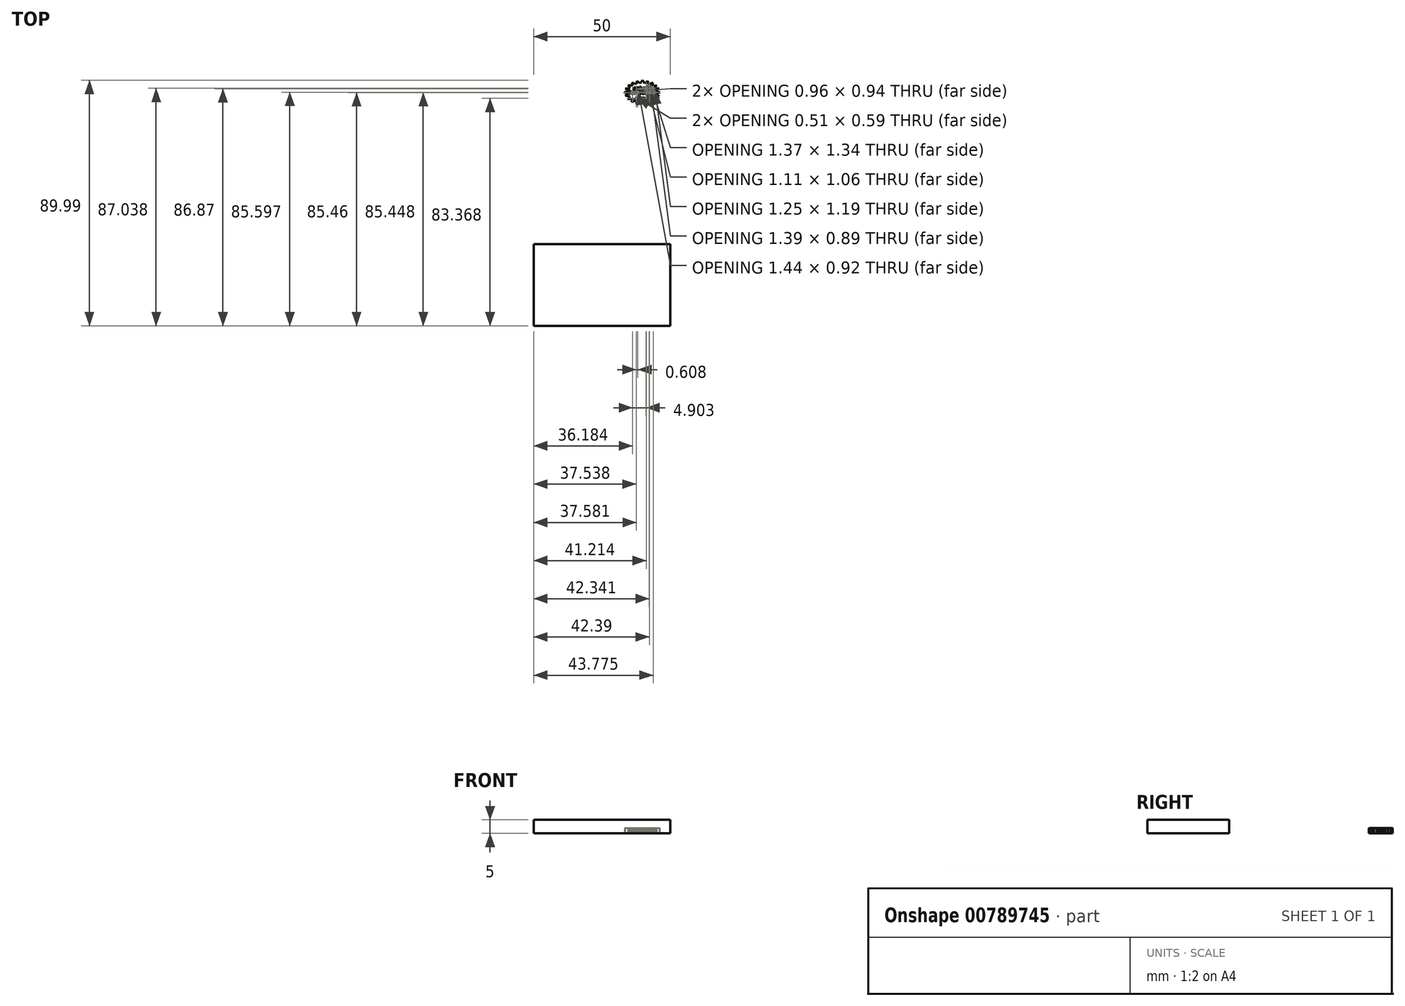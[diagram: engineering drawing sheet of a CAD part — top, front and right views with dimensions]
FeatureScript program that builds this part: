
annotation { "Feature Type Name" : "Feature", "Feature Type Description" : "" }
export const myFeature = defineFeature(function(context is Context, id is Id, definition is map)
    precondition{}
    {
        {
            var Q0;
            Q0=qCreatedBy(makeId("Top.planeOp"),FACE);
            var sketch = newSketch(context, id + "F0", { "sketchPlane" : qUnion([Q0])});
            skLineSegment(sketch, "E0.bottom", {"start": v(-29.78, 14.72) * mm, "end": v(20.22, 14.72) * mm});
            skLineSegment(sketch, "E0.top", {"start": v(-29.78, -15.28) * mm, "end": v(20.22, -15.28) * mm});
            skLineSegment(sketch, "E0.left", {"start": v(-29.78, 14.72) * mm, "end": v(-29.78, -15.28) * mm});
            skLineSegment(sketch, "E0.right", {"start": v(20.22, 14.72) * mm, "end": v(20.22, -15.28) * mm});
            skSolve(sketch);
        }
        {
            var Q0;
            Q0=makeQuery(id+"F0.imprint","IMPRINT",FACE,{"disambiguationData":[TD([[makeQuery(id+"F0.imprint","IMPRINT",EDGE,{"derivedFrom":sQuery(id+"F0.wireOp",EDGE,"E0.bottom")}),-1.0]])]});
            extrude(context, id + "F1", {"entities" : qUnion([Q0]), "depth" : 5 * mm, "offsetDistance" : 25 * mm});
        }
        {
            var Q0;
            Q0=qCreatedBy(makeId("Top.planeOp"),FACE);
            var sketch = newSketch(context, id + "F2", { "sketchPlane" : qUnion([Q0])});
            skLineSegment(sketch, "E1", {"start": v(13.24, 72.43) * mm, "end": v(12.87, 72.43) * mm});
            skLineSegment(sketch, "E2", {"start": v(12.87, 72.43) * mm, "end": v(12.56, 71.95) * mm});
            skLineSegment(sketch, "E3", {"start": v(12.56, 71.95) * mm, "end": v(12.26, 72.43) * mm});
            skLineSegment(sketch, "E4", {"start": v(12.26, 72.43) * mm, "end": v(11.88, 72.43) * mm});
            skLineSegment(sketch, "E5", {"start": v(11.88, 72.43) * mm, "end": v(12.39, 71.65) * mm});
            skLineSegment(sketch, "E6", {"start": v(12.39, 71.65) * mm, "end": v(12.39, 71.09) * mm});
            skLineSegment(sketch, "E7", {"start": v(12.39, 71.09) * mm, "end": v(12.73, 71.09) * mm});
            skLineSegment(sketch, "E8", {"start": v(12.73, 71.09) * mm, "end": v(12.73, 71.65) * mm});
            skLineSegment(sketch, "E9", {"start": v(12.73, 71.65) * mm, "end": v(13.24, 72.43) * mm});
            skFitSpline(sketch, "E10", {"points": [v(11.43, 71.89) * mm, v(11.5, 71.89) * mm, v(11.56, 71.86) * mm, v(11.6, 71.81) * mm]});
            skFitSpline(sketch, "E11", {"points": [v(11.6, 71.81) * mm, v(11.63, 71.76) * mm, v(11.65, 71.69) * mm, v(11.65, 71.59) * mm]});
            skFitSpline(sketch, "E12", {"points": [v(11.65, 71.59) * mm, v(11.65, 71.5) * mm, v(11.63, 71.42) * mm, v(11.6, 71.37) * mm]});
            skFitSpline(sketch, "E13", {"points": [v(11.6, 71.37) * mm, v(11.56, 71.32) * mm, v(11.5, 71.3) * mm, v(11.43, 71.3) * mm]});
            skFitSpline(sketch, "E14", {"points": [v(11.43, 71.3) * mm, v(11.36, 71.3) * mm, v(11.3, 71.32) * mm, v(11.27, 71.37) * mm]});
            skFitSpline(sketch, "E15", {"points": [v(11.27, 71.37) * mm, v(11.23, 71.42) * mm, v(11.22, 71.5) * mm, v(11.22, 71.59) * mm]});
            skFitSpline(sketch, "E16", {"points": [v(11.22, 71.59) * mm, v(11.22, 71.69) * mm, v(11.23, 71.76) * mm, v(11.27, 71.81) * mm]});
            skFitSpline(sketch, "E17", {"points": [v(11.27, 71.81) * mm, v(11.3, 71.86) * mm, v(11.36, 71.89) * mm, v(11.43, 71.89) * mm]});
            skFitSpline(sketch, "E18", {"points": [v(11.43, 72.12) * mm, v(11.26, 72.12) * mm, v(11.12, 72.07) * mm, v(11.03, 71.98) * mm]});
            skFitSpline(sketch, "E19", {"points": [v(11.03, 71.98) * mm, v(10.93, 71.88) * mm, v(10.88, 71.75) * mm, v(10.88, 71.59) * mm]});
            skFitSpline(sketch, "E20", {"points": [v(10.88, 71.59) * mm, v(10.88, 71.42) * mm, v(10.93, 71.3) * mm, v(11.03, 71.2) * mm]});
            skFitSpline(sketch, "E21", {"points": [v(11.03, 71.2) * mm, v(11.12, 71.1) * mm, v(11.26, 71.06) * mm, v(11.43, 71.06) * mm]});
            skFitSpline(sketch, "E22", {"points": [v(11.43, 71.06) * mm, v(11.6, 71.06) * mm, v(11.74, 71.1) * mm, v(11.84, 71.2) * mm]});
            skFitSpline(sketch, "E23", {"points": [v(11.84, 71.2) * mm, v(11.94, 71.3) * mm, v(11.99, 71.42) * mm, v(11.99, 71.59) * mm]});
            skFitSpline(sketch, "E24", {"points": [v(11.99, 71.59) * mm, v(11.99, 71.75) * mm, v(11.94, 71.88) * mm, v(11.84, 71.98) * mm]});
            skFitSpline(sketch, "E25", {"points": [v(11.84, 71.98) * mm, v(11.74, 72.07) * mm, v(11.6, 72.12) * mm, v(11.43, 72.12) * mm]});
            skLineSegment(sketch, "E26", {"start": v(10.66, 71.48) * mm, "end": v(10.66, 72.1) * mm});
            skLineSegment(sketch, "E27", {"start": v(10.66, 72.1) * mm, "end": v(10.34, 72.1) * mm});
            skLineSegment(sketch, "E28", {"start": v(10.34, 72.1) * mm, "end": v(10.34, 72) * mm});
            skFitSpline(sketch, "E29", {"points": [v(10.34, 72) * mm, v(10.34, 71.94) * mm, v(10.34, 71.87) * mm, v(10.34, 71.79) * mm]});
            skFitSpline(sketch, "E30", {"points": [v(10.34, 71.79) * mm, v(10.34, 71.7) * mm, v(10.34, 71.65) * mm, v(10.34, 71.62) * mm]});
            skFitSpline(sketch, "E31", {"points": [v(10.34, 71.62) * mm, v(10.34, 71.54) * mm, v(10.34, 71.48) * mm, v(10.33, 71.45) * mm]});
            skFitSpline(sketch, "E32", {"points": [v(10.33, 71.45) * mm, v(10.33, 71.41) * mm, v(10.32, 71.39) * mm, v(10.3, 71.37) * mm]});
            skFitSpline(sketch, "E33", {"points": [v(10.3, 71.37) * mm, v(10.3, 71.35) * mm, v(10.28, 71.33) * mm, v(10.26, 71.32) * mm]});
            skFitSpline(sketch, "E34", {"points": [v(10.26, 71.32) * mm, v(10.24, 71.31) * mm, v(10.21, 71.3) * mm, v(10.19, 71.3) * mm]});
            skFitSpline(sketch, "E35", {"points": [v(10.19, 71.3) * mm, v(10.12, 71.3) * mm, v(10.07, 71.33) * mm, v(10.03, 71.38) * mm]});
            skFitSpline(sketch, "E36", {"points": [v(10.03, 71.38) * mm, v(9.99, 71.43) * mm, v(9.97, 71.5) * mm, v(9.97, 71.6) * mm]});
            skLineSegment(sketch, "E37", {"start": v(9.97, 71.6) * mm, "end": v(9.97, 72.1) * mm});
            skLineSegment(sketch, "E38", {"start": v(9.97, 72.1) * mm, "end": v(9.65, 72.1) * mm});
            skLineSegment(sketch, "E39", {"start": v(9.65, 72.1) * mm, "end": v(9.65, 71.09) * mm});
            skLineSegment(sketch, "E40", {"start": v(9.65, 71.09) * mm, "end": v(9.97, 71.09) * mm});
            skLineSegment(sketch, "E41", {"start": v(9.97, 71.09) * mm, "end": v(9.97, 71.23) * mm});
            skFitSpline(sketch, "E42", {"points": [v(9.97, 71.23) * mm, v(10.02, 71.18) * mm, v(10.07, 71.13) * mm, v(10.12, 71.1) * mm]});
            skFitSpline(sketch, "E43", {"points": [v(10.12, 71.1) * mm, v(10.18, 71.08) * mm, v(10.24, 71.06) * mm, v(10.3, 71.06) * mm]});
            skFitSpline(sketch, "E44", {"points": [v(10.3, 71.06) * mm, v(10.42, 71.06) * mm, v(10.5, 71.1) * mm, v(10.57, 71.17) * mm]});
            skFitSpline(sketch, "E45", {"points": [v(10.57, 71.17) * mm, v(10.63, 71.24) * mm, v(10.66, 71.34) * mm, v(10.66, 71.48) * mm]});
            skLineSegment(sketch, "E46", {"start": v(9.1, 72.43) * mm, "end": v(9.1, 71.93) * mm});
            skLineSegment(sketch, "E47", {"start": v(9.1, 71.93) * mm, "end": v(9.32, 71.93) * mm});
            skLineSegment(sketch, "E48", {"start": v(9.32, 71.93) * mm, "end": v(9.32, 72.43) * mm});
            skLineSegment(sketch, "E49", {"start": v(9.32, 72.43) * mm, "end": v(9.1, 72.43) * mm});
            skFitSpline(sketch, "E50", {"points": [v(8.03, 71.82) * mm, v(8.06, 71.83) * mm, v(8.09, 71.84) * mm, v(8.11, 71.85) * mm]});
            skFitSpline(sketch, "E51", {"points": [v(8.11, 71.85) * mm, v(8.14, 71.85) * mm, v(8.17, 71.86) * mm, v(8.2, 71.86) * mm]});
            skFitSpline(sketch, "E52", {"points": [v(8.2, 71.86) * mm, v(8.28, 71.86) * mm, v(8.34, 71.83) * mm, v(8.39, 71.78) * mm]});
            skFitSpline(sketch, "E53", {"points": [v(8.39, 71.78) * mm, v(8.43, 71.73) * mm, v(8.45, 71.65) * mm, v(8.45, 71.55) * mm]});
            skLineSegment(sketch, "E54", {"start": v(8.45, 71.55) * mm, "end": v(8.45, 71.09) * mm});
            skLineSegment(sketch, "E55", {"start": v(8.45, 71.09) * mm, "end": v(8.78, 71.09) * mm});
            skLineSegment(sketch, "E56", {"start": v(8.78, 71.09) * mm, "end": v(8.78, 72.1) * mm});
            skLineSegment(sketch, "E57", {"start": v(8.78, 72.1) * mm, "end": v(8.45, 72.1) * mm});
            skLineSegment(sketch, "E58", {"start": v(8.45, 72.1) * mm, "end": v(8.45, 71.93) * mm});
            skFitSpline(sketch, "E59", {"points": [v(8.45, 71.93) * mm, v(8.41, 72) * mm, v(8.37, 72.04) * mm, v(8.31, 72.07) * mm]});
            skFitSpline(sketch, "E60", {"points": [v(8.31, 72.07) * mm, v(8.26, 72.1) * mm, v(8.2, 72.12) * mm, v(8.12, 72.12) * mm]});
            skFitSpline(sketch, "E61", {"points": [v(8.12, 72.12) * mm, v(8.1, 72.12) * mm, v(8.1, 72.12) * mm, v(8.09, 72.12) * mm]});
            skFitSpline(sketch, "E62", {"points": [v(8.09, 72.12) * mm, v(8.07, 72.11) * mm, v(8.05, 72.11) * mm, v(8.03, 72.1) * mm]});
            skLineSegment(sketch, "E63", {"start": v(8.03, 72.1) * mm, "end": v(8.03, 71.82) * mm});
            skLineSegment(sketch, "E64", {"start": v(6.87, 71.6) * mm, "end": v(6.87, 71.5) * mm});
            skLineSegment(sketch, "E65", {"start": v(6.87, 71.5) * mm, "end": v(7.62, 71.5) * mm});
            skFitSpline(sketch, "E66", {"points": [v(7.62, 71.5) * mm, v(7.6, 71.43) * mm, v(7.58, 71.37) * mm, v(7.53, 71.33) * mm]});
            skFitSpline(sketch, "E67", {"points": [v(7.53, 71.33) * mm, v(7.49, 71.3) * mm, v(7.42, 71.28) * mm, v(7.34, 71.28) * mm]});
            skFitSpline(sketch, "E68", {"points": [v(7.34, 71.28) * mm, v(7.27, 71.28) * mm, v(7.2, 71.29) * mm, v(7.13, 71.3) * mm]});
            skFitSpline(sketch, "E69", {"points": [v(7.13, 71.3) * mm, v(7.06, 71.33) * mm, v(6.99, 71.36) * mm, v(6.91, 71.4) * mm]});
            skLineSegment(sketch, "E70", {"start": v(6.91, 71.4) * mm, "end": v(6.91, 71.15) * mm});
            skFitSpline(sketch, "E71", {"points": [v(6.91, 71.15) * mm, v(6.99, 71.12) * mm, v(7.07, 71.1) * mm, v(7.14, 71.09) * mm]});
            skFitSpline(sketch, "E72", {"points": [v(7.14, 71.09) * mm, v(7.22, 71.07) * mm, v(7.3, 71.06) * mm, v(7.37, 71.06) * mm]});
            skFitSpline(sketch, "E73", {"points": [v(7.37, 71.06) * mm, v(7.55, 71.06) * mm, v(7.7, 71.1) * mm, v(7.8, 71.2) * mm]});
            skFitSpline(sketch, "E74", {"points": [v(7.8, 71.2) * mm, v(7.9, 71.3) * mm, v(7.94, 71.42) * mm, v(7.94, 71.59) * mm]});
            skFitSpline(sketch, "E75", {"points": [v(7.94, 71.59) * mm, v(7.94, 71.75) * mm, v(7.9, 71.88) * mm, v(7.8, 71.98) * mm]});
            skFitSpline(sketch, "E76", {"points": [v(7.8, 71.98) * mm, v(7.7, 72.07) * mm, v(7.56, 72.12) * mm, v(7.39, 72.12) * mm]});
            skFitSpline(sketch, "E77", {"points": [v(7.39, 72.12) * mm, v(7.23, 72.12) * mm, v(7.1, 72.07) * mm, v(7, 71.97) * mm]});
            skFitSpline(sketch, "E78", {"points": [v(7, 71.97) * mm, v(6.91, 71.88) * mm, v(6.87, 71.75) * mm, v(6.87, 71.6) * mm]});
            skFitSpline(sketch, "E79", {"points": [v(7.2, 71.7) * mm, v(7.2, 71.76) * mm, v(7.21, 71.81) * mm, v(7.25, 71.85) * mm]});
            skFitSpline(sketch, "E80", {"points": [v(7.25, 71.85) * mm, v(7.28, 71.88) * mm, v(7.33, 71.9) * mm, v(7.39, 71.9) * mm]});
            skFitSpline(sketch, "E81", {"points": [v(7.39, 71.9) * mm, v(7.45, 71.9) * mm, v(7.5, 71.89) * mm, v(7.54, 71.85) * mm]});
            skFitSpline(sketch, "E82", {"points": [v(7.54, 71.85) * mm, v(7.58, 71.82) * mm, v(7.6, 71.77) * mm, v(7.61, 71.7) * mm]});
            skLineSegment(sketch, "E83", {"start": v(7.61, 71.7) * mm, "end": v(7.2, 71.7) * mm});
            skLineSegment(sketch, "E84", {"start": v(15.2, 67.7) * mm, "end": v(13.44, 67.93) * mm});
            skLineSegment(sketch, "E85", {"start": v(13.44, 67.93) * mm, "end": v(13.75, 66.73) * mm});
            skLineSegment(sketch, "E86", {"start": v(13.75, 66.73) * mm, "end": v(12.18, 67.32) * mm});
            skLineSegment(sketch, "E87", {"start": v(12.18, 67.32) * mm, "end": v(11.92, 66.12) * mm});
            skLineSegment(sketch, "E88", {"start": v(11.92, 66.12) * mm, "end": v(10.7, 67) * mm});
            skLineSegment(sketch, "E89", {"start": v(10.7, 67) * mm, "end": v(9.9, 65.92) * mm});
            skLineSegment(sketch, "E90", {"start": v(9.9, 65.92) * mm, "end": v(9.14, 67.02) * mm});
            skLineSegment(sketch, "E91", {"start": v(9.14, 67.02) * mm, "end": v(7.9, 66.15) * mm});
            skLineSegment(sketch, "E92", {"start": v(7.9, 66.15) * mm, "end": v(7.67, 67.35) * mm});
            skLineSegment(sketch, "E93", {"start": v(7.67, 67.35) * mm, "end": v(6.08, 66.78) * mm});
            skLineSegment(sketch, "E94", {"start": v(6.08, 66.78) * mm, "end": v(6.43, 67.97) * mm});
            skLineSegment(sketch, "E95", {"start": v(6.43, 67.97) * mm, "end": v(4.65, 67.76) * mm});
            skLineSegment(sketch, "E96", {"start": v(4.65, 67.76) * mm, "end": v(5.53, 68.82) * mm});
            skLineSegment(sketch, "E97", {"start": v(5.53, 68.82) * mm, "end": v(3.74, 69) * mm});
            skLineSegment(sketch, "E98", {"start": v(3.74, 69) * mm, "end": v(5.06, 69.82) * mm});
            skLineSegment(sketch, "E99", {"start": v(5.06, 69.82) * mm, "end": v(3.44, 70.36) * mm});
            skLineSegment(sketch, "E100", {"start": v(3.44, 70.36) * mm, "end": v(5.08, 70.87) * mm});
            skLineSegment(sketch, "E101", {"start": v(5.08, 70.87) * mm, "end": v(3.78, 71.71) * mm});
            skLineSegment(sketch, "E102", {"start": v(3.78, 71.71) * mm, "end": v(5.57, 71.86) * mm});
            skLineSegment(sketch, "E103", {"start": v(5.57, 71.86) * mm, "end": v(4.73, 72.93) * mm});
            skLineSegment(sketch, "E104", {"start": v(4.73, 72.93) * mm, "end": v(6.5, 72.7) * mm});
            skLineSegment(sketch, "E105", {"start": v(6.5, 72.7) * mm, "end": v(6.18, 73.9) * mm});
            skLineSegment(sketch, "E106", {"start": v(6.18, 73.9) * mm, "end": v(7.76, 73.3) * mm});
            skLineSegment(sketch, "E107", {"start": v(7.76, 73.3) * mm, "end": v(8.01, 74.5) * mm});
            skLineSegment(sketch, "E108", {"start": v(8.01, 74.5) * mm, "end": v(9.24, 73.62) * mm});
            skLineSegment(sketch, "E109", {"start": v(9.24, 73.62) * mm, "end": v(10.03, 74.7) * mm});
            skLineSegment(sketch, "E110", {"start": v(10.03, 74.7) * mm, "end": v(10.8, 73.6) * mm});
            skLineSegment(sketch, "E111", {"start": v(10.8, 73.6) * mm, "end": v(12.05, 74.48) * mm});
            skLineSegment(sketch, "E112", {"start": v(12.05, 74.48) * mm, "end": v(12.26, 73.27) * mm});
            skLineSegment(sketch, "E113", {"start": v(12.26, 73.27) * mm, "end": v(13.86, 73.84) * mm});
            skLineSegment(sketch, "E114", {"start": v(13.86, 73.84) * mm, "end": v(13.5, 72.65) * mm});
            skLineSegment(sketch, "E115", {"start": v(13.5, 72.65) * mm, "end": v(15.29, 72.86) * mm});
            skLineSegment(sketch, "E116", {"start": v(15.29, 72.86) * mm, "end": v(14.4, 71.8) * mm});
            skLineSegment(sketch, "E117", {"start": v(14.4, 71.8) * mm, "end": v(16.2, 71.63) * mm});
            skLineSegment(sketch, "E118", {"start": v(16.2, 71.63) * mm, "end": v(14.87, 70.8) * mm});
            skLineSegment(sketch, "E119", {"start": v(14.87, 70.8) * mm, "end": v(16.5, 70.27) * mm});
            skLineSegment(sketch, "E120", {"start": v(16.5, 70.27) * mm, "end": v(14.86, 69.76) * mm});
            skLineSegment(sketch, "E121", {"start": v(14.86, 69.76) * mm, "end": v(16.15, 68.91) * mm});
            skLineSegment(sketch, "E122", {"start": v(16.15, 68.91) * mm, "end": v(14.37, 68.77) * mm});
            skLineSegment(sketch, "E123", {"start": v(14.37, 68.77) * mm, "end": v(15.2, 67.7) * mm});
            skLineSegment(sketch, "E124", {"start": v(13.75, 69.94) * mm, "end": v(14.23, 69.94) * mm});
            skLineSegment(sketch, "E125", {"start": v(14.23, 69.94) * mm, "end": v(14.3, 69.72) * mm});
            skLineSegment(sketch, "E126", {"start": v(14.3, 69.72) * mm, "end": v(14.62, 69.72) * mm});
            skLineSegment(sketch, "E127", {"start": v(14.62, 69.72) * mm, "end": v(14.18, 70.91) * mm});
            skLineSegment(sketch, "E128", {"start": v(14.18, 70.91) * mm, "end": v(13.81, 70.91) * mm});
            skLineSegment(sketch, "E129", {"start": v(13.81, 70.91) * mm, "end": v(13.37, 69.72) * mm});
            skLineSegment(sketch, "E130", {"start": v(13.37, 69.72) * mm, "end": v(13.68, 69.72) * mm});
            skLineSegment(sketch, "E131", {"start": v(13.68, 69.72) * mm, "end": v(13.75, 69.94) * mm});
            skLineSegment(sketch, "E132", {"start": v(14.16, 70.16) * mm, "end": v(13.83, 70.16) * mm});
            skLineSegment(sketch, "E133", {"start": v(13.83, 70.16) * mm, "end": v(14, 70.63) * mm});
            skLineSegment(sketch, "E134", {"start": v(14, 70.63) * mm, "end": v(14.16, 70.16) * mm});
            skLineSegment(sketch, "E135", {"start": v(13.3, 70.61) * mm, "end": v(13.03, 70.61) * mm});
            skLineSegment(sketch, "E136", {"start": v(13.03, 70.61) * mm, "end": v(12.88, 70) * mm});
            skLineSegment(sketch, "E137", {"start": v(12.88, 70) * mm, "end": v(12.73, 70.61) * mm});
            skLineSegment(sketch, "E138", {"start": v(12.73, 70.61) * mm, "end": v(12.5, 70.61) * mm});
            skLineSegment(sketch, "E139", {"start": v(12.5, 70.61) * mm, "end": v(12.34, 70) * mm});
            skLineSegment(sketch, "E140", {"start": v(12.34, 70) * mm, "end": v(12.2, 70.61) * mm});
            skLineSegment(sketch, "E141", {"start": v(12.2, 70.61) * mm, "end": v(11.91, 70.61) * mm});
            skLineSegment(sketch, "E142", {"start": v(11.91, 70.61) * mm, "end": v(12.15, 69.72) * mm});
            skLineSegment(sketch, "E143", {"start": v(12.15, 69.72) * mm, "end": v(12.46, 69.72) * mm});
            skLineSegment(sketch, "E144", {"start": v(12.46, 69.72) * mm, "end": v(12.61, 70.34) * mm});
            skLineSegment(sketch, "E145", {"start": v(12.61, 70.34) * mm, "end": v(12.76, 69.72) * mm});
            skLineSegment(sketch, "E146", {"start": v(12.76, 69.72) * mm, "end": v(13.07, 69.72) * mm});
            skLineSegment(sketch, "E147", {"start": v(13.07, 69.72) * mm, "end": v(13.3, 70.61) * mm});
            skLineSegment(sketch, "E148", {"start": v(10.83, 70.17) * mm, "end": v(10.83, 70.09) * mm});
            skLineSegment(sketch, "E149", {"start": v(10.83, 70.09) * mm, "end": v(11.5, 70.09) * mm});
            skFitSpline(sketch, "E150", {"points": [v(11.5, 70.09) * mm, v(11.49, 70.02) * mm, v(11.46, 69.97) * mm, v(11.42, 69.94) * mm]});
            skFitSpline(sketch, "E151", {"points": [v(11.42, 69.94) * mm, v(11.38, 69.9) * mm, v(11.32, 69.89) * mm, v(11.25, 69.89) * mm]});
            skFitSpline(sketch, "E152", {"points": [v(11.25, 69.89) * mm, v(11.19, 69.89) * mm, v(11.13, 69.9) * mm, v(11.06, 69.91) * mm]});
            skFitSpline(sketch, "E153", {"points": [v(11.06, 69.91) * mm, v(11, 69.93) * mm, v(10.94, 69.96) * mm, v(10.87, 70) * mm]});
            skLineSegment(sketch, "E154", {"start": v(10.87, 70) * mm, "end": v(10.87, 69.78) * mm});
            skFitSpline(sketch, "E155", {"points": [v(10.87, 69.78) * mm, v(10.94, 69.75) * mm, v(11, 69.73) * mm, v(11.07, 69.72) * mm]});
            skFitSpline(sketch, "E156", {"points": [v(11.07, 69.72) * mm, v(11.14, 69.7) * mm, v(11.2, 69.7) * mm, v(11.28, 69.7) * mm]});
            skFitSpline(sketch, "E157", {"points": [v(11.28, 69.7) * mm, v(11.44, 69.7) * mm, v(11.56, 69.74) * mm, v(11.65, 69.82) * mm]});
            skFitSpline(sketch, "E158", {"points": [v(11.65, 69.82) * mm, v(11.74, 69.9) * mm, v(11.79, 70.02) * mm, v(11.79, 70.17) * mm]});
            skFitSpline(sketch, "E159", {"points": [v(11.79, 70.17) * mm, v(11.79, 70.31) * mm, v(11.74, 70.43) * mm, v(11.65, 70.51) * mm]});
            skFitSpline(sketch, "E160", {"points": [v(11.65, 70.51) * mm, v(11.57, 70.6) * mm, v(11.45, 70.64) * mm, v(11.3, 70.64) * mm]});
            skFitSpline(sketch, "E161", {"points": [v(11.3, 70.64) * mm, v(11.15, 70.64) * mm, v(11.04, 70.6) * mm, v(10.95, 70.5) * mm]});
            skFitSpline(sketch, "E162", {"points": [v(10.95, 70.5) * mm, v(10.87, 70.42) * mm, v(10.83, 70.31) * mm, v(10.83, 70.17) * mm]});
            skFitSpline(sketch, "E163", {"points": [v(11.12, 70.27) * mm, v(11.12, 70.32) * mm, v(11.14, 70.36) * mm, v(11.17, 70.4) * mm]});
            skFitSpline(sketch, "E164", {"points": [v(11.17, 70.4) * mm, v(11.2, 70.43) * mm, v(11.24, 70.45) * mm, v(11.3, 70.45) * mm]});
            skFitSpline(sketch, "E165", {"points": [v(11.3, 70.45) * mm, v(11.35, 70.45) * mm, v(11.4, 70.43) * mm, v(11.43, 70.4) * mm]});
            skFitSpline(sketch, "E166", {"points": [v(11.43, 70.4) * mm, v(11.46, 70.37) * mm, v(11.48, 70.32) * mm, v(11.5, 70.27) * mm]});
            skLineSegment(sketch, "E167", {"start": v(11.5, 70.27) * mm, "end": v(11.12, 70.27) * mm});
            skLineSegment(sketch, "E168", {"start": v(9.92, 70.59) * mm, "end": v(9.92, 70.37) * mm});
            skFitSpline(sketch, "E169", {"points": [v(9.92, 70.37) * mm, v(9.98, 70.4) * mm, v(10.04, 70.41) * mm, v(10.1, 70.43) * mm]});
            skFitSpline(sketch, "E170", {"points": [v(10.1, 70.43) * mm, v(10.15, 70.44) * mm, v(10.2, 70.45) * mm, v(10.25, 70.45) * mm]});
            skFitSpline(sketch, "E171", {"points": [v(10.25, 70.45) * mm, v(10.3, 70.45) * mm, v(10.35, 70.44) * mm, v(10.37, 70.43) * mm]});
            skFitSpline(sketch, "E172", {"points": [v(10.37, 70.43) * mm, v(10.4, 70.41) * mm, v(10.41, 70.4) * mm, v(10.41, 70.36) * mm]});
            skFitSpline(sketch, "E173", {"points": [v(10.41, 70.36) * mm, v(10.41, 70.34) * mm, v(10.4, 70.32) * mm, v(10.38, 70.31) * mm]});
            skFitSpline(sketch, "E174", {"points": [v(10.38, 70.31) * mm, v(10.36, 70.3) * mm, v(10.33, 70.29) * mm, v(10.28, 70.28) * mm]});
            skLineSegment(sketch, "E175", {"start": v(10.28, 70.28) * mm, "end": v(10.23, 70.28) * mm});
            skFitSpline(sketch, "E176", {"points": [v(10.23, 70.28) * mm, v(10.08, 70.26) * mm, v(9.98, 70.23) * mm, v(9.93, 70.19) * mm]});
            skFitSpline(sketch, "E177", {"points": [v(9.93, 70.19) * mm, v(9.88, 70.14) * mm, v(9.86, 70.08) * mm, v(9.86, 69.99) * mm]});
            skFitSpline(sketch, "E178", {"points": [v(9.86, 69.99) * mm, v(9.86, 69.89) * mm, v(9.9, 69.82) * mm, v(9.96, 69.77) * mm]});
            skFitSpline(sketch, "E179", {"points": [v(9.96, 69.77) * mm, v(10.03, 69.72) * mm, v(10.14, 69.7) * mm, v(10.28, 69.7) * mm]});
            skFitSpline(sketch, "E180", {"points": [v(10.28, 69.7) * mm, v(10.33, 69.7) * mm, v(10.4, 69.7) * mm, v(10.46, 69.71) * mm]});
            skFitSpline(sketch, "E181", {"points": [v(10.46, 69.71) * mm, v(10.52, 69.72) * mm, v(10.59, 69.74) * mm, v(10.65, 69.75) * mm]});
            skLineSegment(sketch, "E182", {"start": v(10.65, 69.75) * mm, "end": v(10.65, 69.97) * mm});
            skFitSpline(sketch, "E183", {"points": [v(10.65, 69.97) * mm, v(10.6, 69.94) * mm, v(10.54, 69.92) * mm, v(10.48, 69.9) * mm]});
            skFitSpline(sketch, "E184", {"points": [v(10.48, 69.9) * mm, v(10.42, 69.9) * mm, v(10.36, 69.89) * mm, v(10.3, 69.89) * mm]});
            skFitSpline(sketch, "E185", {"points": [v(10.3, 69.89) * mm, v(10.24, 69.89) * mm, v(10.2, 69.9) * mm, v(10.17, 69.91) * mm]});
            skFitSpline(sketch, "E186", {"points": [v(10.17, 69.91) * mm, v(10.14, 69.93) * mm, v(10.13, 69.95) * mm, v(10.13, 69.98) * mm]});
            skFitSpline(sketch, "E187", {"points": [v(10.13, 69.98) * mm, v(10.13, 70) * mm, v(10.14, 70.02) * mm, v(10.16, 70.04) * mm]});
            skFitSpline(sketch, "E188", {"points": [v(10.16, 70.04) * mm, v(10.18, 70.05) * mm, v(10.21, 70.06) * mm, v(10.27, 70.07) * mm]});
            skLineSegment(sketch, "E189", {"start": v(10.27, 70.07) * mm, "end": v(10.32, 70.07) * mm});
            skFitSpline(sketch, "E190", {"points": [v(10.32, 70.07) * mm, v(10.45, 70.09) * mm, v(10.54, 70.12) * mm, v(10.59, 70.16) * mm]});
            skFitSpline(sketch, "E191", {"points": [v(10.59, 70.16) * mm, v(10.64, 70.2) * mm, v(10.67, 70.27) * mm, v(10.67, 70.36) * mm]});
            skFitSpline(sketch, "E192", {"points": [v(10.67, 70.36) * mm, v(10.67, 70.45) * mm, v(10.63, 70.52) * mm, v(10.57, 70.57) * mm]});
            skFitSpline(sketch, "E193", {"points": [v(10.57, 70.57) * mm, v(10.5, 70.61) * mm, v(10.4, 70.64) * mm, v(10.27, 70.64) * mm]});
            skFitSpline(sketch, "E194", {"points": [v(10.27, 70.64) * mm, v(10.22, 70.64) * mm, v(10.16, 70.63) * mm, v(10.1, 70.62) * mm]});
            skFitSpline(sketch, "E195", {"points": [v(10.1, 70.62) * mm, v(10.05, 70.62) * mm, v(9.98, 70.6) * mm, v(9.92, 70.59) * mm]});
            skFitSpline(sketch, "E196", {"points": [v(9.22, 70.43) * mm, v(9.28, 70.43) * mm, v(9.33, 70.4) * mm, v(9.36, 70.36) * mm]});
            skFitSpline(sketch, "E197", {"points": [v(9.36, 70.36) * mm, v(9.4, 70.32) * mm, v(9.41, 70.25) * mm, v(9.41, 70.17) * mm]});
            skFitSpline(sketch, "E198", {"points": [v(9.41, 70.17) * mm, v(9.41, 70.08) * mm, v(9.4, 70.02) * mm, v(9.36, 69.97) * mm]});
            skFitSpline(sketch, "E199", {"points": [v(9.36, 69.97) * mm, v(9.33, 69.93) * mm, v(9.28, 69.9) * mm, v(9.22, 69.9) * mm]});
            skFitSpline(sketch, "E200", {"points": [v(9.22, 69.9) * mm, v(9.15, 69.9) * mm, v(9.1, 69.93) * mm, v(9.07, 69.97) * mm]});
            skFitSpline(sketch, "E201", {"points": [v(9.07, 69.97) * mm, v(9.04, 70.02) * mm, v(9.02, 70.08) * mm, v(9.02, 70.17) * mm]});
            skFitSpline(sketch, "E202", {"points": [v(9.02, 70.17) * mm, v(9.02, 70.25) * mm, v(9.04, 70.32) * mm, v(9.07, 70.36) * mm]});
            skFitSpline(sketch, "E203", {"points": [v(9.07, 70.36) * mm, v(9.1, 70.4) * mm, v(9.15, 70.43) * mm, v(9.22, 70.43) * mm]});
            skFitSpline(sketch, "E204", {"points": [v(9.22, 70.64) * mm, v(9.06, 70.64) * mm, v(8.94, 70.6) * mm, v(8.86, 70.51) * mm]});
            skFitSpline(sketch, "E205", {"points": [v(8.86, 70.51) * mm, v(8.77, 70.43) * mm, v(8.73, 70.31) * mm, v(8.73, 70.17) * mm]});
            skFitSpline(sketch, "E206", {"points": [v(8.73, 70.17) * mm, v(8.73, 70.02) * mm, v(8.77, 69.9) * mm, v(8.86, 69.82) * mm]});
            skFitSpline(sketch, "E207", {"points": [v(8.86, 69.82) * mm, v(8.94, 69.74) * mm, v(9.06, 69.7) * mm, v(9.22, 69.7) * mm]});
            skFitSpline(sketch, "E208", {"points": [v(9.22, 69.7) * mm, v(9.37, 69.7) * mm, v(9.5, 69.74) * mm, v(9.58, 69.82) * mm]});
            skFitSpline(sketch, "E209", {"points": [v(9.58, 69.82) * mm, v(9.66, 69.9) * mm, v(9.7, 70.02) * mm, v(9.7, 70.17) * mm]});
            skFitSpline(sketch, "E210", {"points": [v(9.7, 70.17) * mm, v(9.7, 70.31) * mm, v(9.66, 70.43) * mm, v(9.58, 70.51) * mm]});
            skFitSpline(sketch, "E211", {"points": [v(9.58, 70.51) * mm, v(9.5, 70.6) * mm, v(9.37, 70.64) * mm, v(9.22, 70.64) * mm]});
            skFitSpline(sketch, "E212", {"points": [v(7.7, 70.47) * mm, v(7.66, 70.52) * mm, v(7.61, 70.56) * mm, v(7.56, 70.6) * mm]});
            skFitSpline(sketch, "E213", {"points": [v(7.56, 70.6) * mm, v(7.51, 70.62) * mm, v(7.46, 70.64) * mm, v(7.4, 70.64) * mm]});
            skFitSpline(sketch, "E214", {"points": [v(7.4, 70.64) * mm, v(7.3, 70.64) * mm, v(7.22, 70.6) * mm, v(7.16, 70.54) * mm]});
            skFitSpline(sketch, "E215", {"points": [v(7.16, 70.54) * mm, v(7.11, 70.48) * mm, v(7.08, 70.39) * mm, v(7.08, 70.27) * mm]});
            skLineSegment(sketch, "E216", {"start": v(7.08, 70.27) * mm, "end": v(7.08, 69.72) * mm});
            skLineSegment(sketch, "E217", {"start": v(7.08, 69.72) * mm, "end": v(7.37, 69.72) * mm});
            skLineSegment(sketch, "E218", {"start": v(7.37, 69.72) * mm, "end": v(7.37, 70.19) * mm});
            skFitSpline(sketch, "E219", {"points": [v(7.37, 70.19) * mm, v(7.37, 70.2) * mm, v(7.37, 70.2) * mm, v(7.37, 70.2) * mm]});
            skFitSpline(sketch, "E220", {"points": [v(7.37, 70.2) * mm, v(7.37, 70.22) * mm, v(7.37, 70.23) * mm, v(7.37, 70.24) * mm]});
            skFitSpline(sketch, "E221", {"points": [v(7.37, 70.24) * mm, v(7.37, 70.3) * mm, v(7.38, 70.35) * mm, v(7.4, 70.38) * mm]});
            skFitSpline(sketch, "E222", {"points": [v(7.4, 70.38) * mm, v(7.42, 70.4) * mm, v(7.45, 70.42) * mm, v(7.49, 70.42) * mm]});
            skFitSpline(sketch, "E223", {"points": [v(7.49, 70.42) * mm, v(7.54, 70.42) * mm, v(7.58, 70.4) * mm, v(7.61, 70.35) * mm]});
            skFitSpline(sketch, "E224", {"points": [v(7.61, 70.35) * mm, v(7.64, 70.3) * mm, v(7.66, 70.24) * mm, v(7.66, 70.16) * mm]});
            skLineSegment(sketch, "E225", {"start": v(7.66, 70.16) * mm, "end": v(7.66, 69.72) * mm});
            skLineSegment(sketch, "E226", {"start": v(7.66, 69.72) * mm, "end": v(7.95, 69.72) * mm});
            skLineSegment(sketch, "E227", {"start": v(7.95, 69.72) * mm, "end": v(7.95, 70.19) * mm});
            skFitSpline(sketch, "E228", {"points": [v(7.95, 70.19) * mm, v(7.95, 70.29) * mm, v(7.95, 70.35) * mm, v(7.97, 70.38) * mm]});
            skFitSpline(sketch, "E229", {"points": [v(7.97, 70.38) * mm, v(7.99, 70.4) * mm, v(8.02, 70.42) * mm, v(8.06, 70.42) * mm]});
            skFitSpline(sketch, "E230", {"points": [v(8.06, 70.42) * mm, v(8.12, 70.42) * mm, v(8.16, 70.4) * mm, v(8.19, 70.35) * mm]});
            skFitSpline(sketch, "E231", {"points": [v(8.19, 70.35) * mm, v(8.22, 70.3) * mm, v(8.23, 70.24) * mm, v(8.23, 70.16) * mm]});
            skLineSegment(sketch, "E232", {"start": v(8.23, 70.16) * mm, "end": v(8.23, 69.72) * mm});
            skLineSegment(sketch, "E233", {"start": v(8.23, 69.72) * mm, "end": v(8.52, 69.72) * mm});
            skLineSegment(sketch, "E234", {"start": v(8.52, 69.72) * mm, "end": v(8.52, 70.61) * mm});
            skLineSegment(sketch, "E235", {"start": v(8.52, 70.61) * mm, "end": v(8.23, 70.61) * mm});
            skLineSegment(sketch, "E236", {"start": v(8.23, 70.61) * mm, "end": v(8.23, 70.48) * mm});
            skFitSpline(sketch, "E237", {"points": [v(8.23, 70.48) * mm, v(8.2, 70.53) * mm, v(8.16, 70.57) * mm, v(8.11, 70.6) * mm]});
            skFitSpline(sketch, "E238", {"points": [v(8.11, 70.6) * mm, v(8.07, 70.62) * mm, v(8.02, 70.64) * mm, v(7.96, 70.64) * mm]});
            skFitSpline(sketch, "E239", {"points": [v(7.96, 70.64) * mm, v(7.9, 70.64) * mm, v(7.85, 70.62) * mm, v(7.8, 70.6) * mm]});
            skFitSpline(sketch, "E240", {"points": [v(7.8, 70.6) * mm, v(7.75, 70.56) * mm, v(7.72, 70.52) * mm, v(7.7, 70.47) * mm]});
            skLineSegment(sketch, "E241", {"start": v(5.93, 70.17) * mm, "end": v(5.93, 70.09) * mm});
            skLineSegment(sketch, "E242", {"start": v(5.93, 70.09) * mm, "end": v(6.6, 70.09) * mm});
            skFitSpline(sketch, "E243", {"points": [v(6.6, 70.09) * mm, v(6.59, 70.02) * mm, v(6.56, 69.97) * mm, v(6.52, 69.94) * mm]});
            skFitSpline(sketch, "E244", {"points": [v(6.52, 69.94) * mm, v(6.48, 69.9) * mm, v(6.42, 69.89) * mm, v(6.35, 69.89) * mm]});
            skFitSpline(sketch, "E245", {"points": [v(6.35, 69.89) * mm, v(6.29, 69.89) * mm, v(6.22, 69.9) * mm, v(6.16, 69.91) * mm]});
            skFitSpline(sketch, "E246", {"points": [v(6.16, 69.91) * mm, v(6.1, 69.93) * mm, v(6.03, 69.96) * mm, v(5.97, 70) * mm]});
            skLineSegment(sketch, "E247", {"start": v(5.97, 70) * mm, "end": v(5.97, 69.78) * mm});
            skFitSpline(sketch, "E248", {"points": [v(5.97, 69.78) * mm, v(6.04, 69.75) * mm, v(6.1, 69.73) * mm, v(6.17, 69.72) * mm]});
            skFitSpline(sketch, "E249", {"points": [v(6.17, 69.72) * mm, v(6.24, 69.7) * mm, v(6.3, 69.7) * mm, v(6.37, 69.7) * mm]});
            skFitSpline(sketch, "E250", {"points": [v(6.37, 69.7) * mm, v(6.53, 69.7) * mm, v(6.66, 69.74) * mm, v(6.75, 69.82) * mm]});
            skFitSpline(sketch, "E251", {"points": [v(6.75, 69.82) * mm, v(6.84, 69.9) * mm, v(6.88, 70.02) * mm, v(6.88, 70.17) * mm]});
            skFitSpline(sketch, "E252", {"points": [v(6.88, 70.17) * mm, v(6.88, 70.31) * mm, v(6.84, 70.43) * mm, v(6.75, 70.51) * mm]});
            skFitSpline(sketch, "E253", {"points": [v(6.75, 70.51) * mm, v(6.66, 70.6) * mm, v(6.54, 70.64) * mm, v(6.39, 70.64) * mm]});
            skFitSpline(sketch, "E254", {"points": [v(6.39, 70.64) * mm, v(6.25, 70.64) * mm, v(6.14, 70.6) * mm, v(6.05, 70.5) * mm]});
            skFitSpline(sketch, "E255", {"points": [v(6.05, 70.5) * mm, v(5.97, 70.42) * mm, v(5.93, 70.31) * mm, v(5.93, 70.17) * mm]});
            skFitSpline(sketch, "E256", {"points": [v(6.22, 70.27) * mm, v(6.22, 70.32) * mm, v(6.23, 70.36) * mm, v(6.27, 70.4) * mm]});
            skFitSpline(sketch, "E257", {"points": [v(6.27, 70.4) * mm, v(6.3, 70.43) * mm, v(6.34, 70.45) * mm, v(6.39, 70.45) * mm]});
            skFitSpline(sketch, "E258", {"points": [v(6.39, 70.45) * mm, v(6.45, 70.45) * mm, v(6.5, 70.43) * mm, v(6.52, 70.4) * mm]});
            skFitSpline(sketch, "E259", {"points": [v(6.52, 70.4) * mm, v(6.56, 70.37) * mm, v(6.58, 70.32) * mm, v(6.59, 70.27) * mm]});
            skLineSegment(sketch, "E260", {"start": v(6.59, 70.27) * mm, "end": v(6.22, 70.27) * mm});
            skLineSegment(sketch, "E261", {"start": v(5.62, 70.91) * mm, "end": v(5.33, 70.91) * mm});
            skLineSegment(sketch, "E262", {"start": v(5.33, 70.91) * mm, "end": v(5.33, 70.46) * mm});
            skLineSegment(sketch, "E263", {"start": v(5.33, 70.46) * mm, "end": v(5.37, 70.12) * mm});
            skLineSegment(sketch, "E264", {"start": v(5.37, 70.12) * mm, "end": v(5.58, 70.12) * mm});
            skLineSegment(sketch, "E265", {"start": v(5.58, 70.12) * mm, "end": v(5.62, 70.46) * mm});
            skLineSegment(sketch, "E266", {"start": v(5.62, 70.46) * mm, "end": v(5.62, 70.91) * mm});
            skLineSegment(sketch, "E267", {"start": v(5.62, 70) * mm, "end": v(5.33, 70) * mm});
            skLineSegment(sketch, "E268", {"start": v(5.33, 70) * mm, "end": v(5.33, 69.72) * mm});
            skLineSegment(sketch, "E269", {"start": v(5.33, 69.72) * mm, "end": v(5.62, 69.72) * mm});
            skLineSegment(sketch, "E270", {"start": v(5.62, 69.72) * mm, "end": v(5.62, 70) * mm});
            skLineSegment(sketch, "E271", {"start": v(11.46, 68.55) * mm, "end": v(11.27, 68.55) * mm});
            skLineSegment(sketch, "E272", {"start": v(11.27, 68.55) * mm, "end": v(11.27, 67.8) * mm});
            skLineSegment(sketch, "E273", {"start": v(11.27, 67.8) * mm, "end": v(11.46, 67.8) * mm});
            skLineSegment(sketch, "E274", {"start": v(11.46, 67.8) * mm, "end": v(11.46, 68.55) * mm});
            skFitSpline(sketch, "E275", {"points": [v(10.36, 67.9) * mm, v(10.38, 67.87) * mm, v(10.4, 67.85) * mm, v(10.44, 67.83) * mm]});
            skFitSpline(sketch, "E276", {"points": [v(10.44, 67.83) * mm, v(10.47, 67.82) * mm, v(10.5, 67.8) * mm, v(10.54, 67.8) * mm]});
            skFitSpline(sketch, "E277", {"points": [v(10.54, 67.8) * mm, v(10.6, 67.8) * mm, v(10.66, 67.84) * mm, v(10.7, 67.9) * mm]});
            skFitSpline(sketch, "E278", {"points": [v(10.7, 67.9) * mm, v(10.75, 67.94) * mm, v(10.78, 68.01) * mm, v(10.78, 68.1) * mm]});
            skFitSpline(sketch, "E279", {"points": [v(10.78, 68.1) * mm, v(10.78, 68.18) * mm, v(10.75, 68.25) * mm, v(10.7, 68.3) * mm]});
            skFitSpline(sketch, "E280", {"points": [v(10.7, 68.3) * mm, v(10.66, 68.35) * mm, v(10.6, 68.38) * mm, v(10.54, 68.38) * mm]});
            skFitSpline(sketch, "E281", {"points": [v(10.54, 68.38) * mm, v(10.5, 68.38) * mm, v(10.47, 68.37) * mm, v(10.44, 68.36) * mm]});
            skFitSpline(sketch, "E282", {"points": [v(10.44, 68.36) * mm, v(10.4, 68.34) * mm, v(10.38, 68.32) * mm, v(10.36, 68.29) * mm]});
            skLineSegment(sketch, "E283", {"start": v(10.36, 68.29) * mm, "end": v(10.36, 68.37) * mm});
            skLineSegment(sketch, "E284", {"start": v(10.36, 68.37) * mm, "end": v(10.18, 68.37) * mm});
            skLineSegment(sketch, "E285", {"start": v(10.18, 68.37) * mm, "end": v(10.18, 67.87) * mm});
            skFitSpline(sketch, "E286", {"points": [v(10.18, 67.87) * mm, v(10.18, 67.78) * mm, v(10.2, 67.7) * mm, v(10.26, 67.66) * mm]});
            skFitSpline(sketch, "E287", {"points": [v(10.26, 67.66) * mm, v(10.32, 67.61) * mm, v(10.4, 67.59) * mm, v(10.5, 67.59) * mm]});
            skFitSpline(sketch, "E288", {"points": [v(10.5, 67.59) * mm, v(10.54, 67.59) * mm, v(10.58, 67.6) * mm, v(10.6, 67.6) * mm]});
            skFitSpline(sketch, "E289", {"points": [v(10.6, 67.6) * mm, v(10.64, 67.6) * mm, v(10.67, 67.61) * mm, v(10.7, 67.62) * mm]});
            skLineSegment(sketch, "E290", {"start": v(10.7, 67.62) * mm, "end": v(10.7, 67.76) * mm});
            skFitSpline(sketch, "E291", {"points": [v(10.7, 67.76) * mm, v(10.68, 67.74) * mm, v(10.65, 67.73) * mm, v(10.62, 67.72) * mm]});
            skFitSpline(sketch, "E292", {"points": [v(10.62, 67.72) * mm, v(10.59, 67.71) * mm, v(10.56, 67.7) * mm, v(10.53, 67.7) * mm]});
            skFitSpline(sketch, "E293", {"points": [v(10.53, 67.7) * mm, v(10.47, 67.7) * mm, v(10.42, 67.72) * mm, v(10.4, 67.75) * mm]});
            skFitSpline(sketch, "E294", {"points": [v(10.4, 67.75) * mm, v(10.37, 67.77) * mm, v(10.36, 67.81) * mm, v(10.36, 67.87) * mm]});
            skLineSegment(sketch, "E295", {"start": v(10.36, 67.87) * mm, "end": v(10.36, 67.9) * mm});
            skFitSpline(sketch, "E296", {"points": [v(10.47, 68.25) * mm, v(10.51, 68.25) * mm, v(10.54, 68.24) * mm, v(10.56, 68.21) * mm]});
            skFitSpline(sketch, "E297", {"points": [v(10.56, 68.21) * mm, v(10.58, 68.18) * mm, v(10.6, 68.15) * mm, v(10.6, 68.1) * mm]});
            skFitSpline(sketch, "E298", {"points": [v(10.6, 68.1) * mm, v(10.6, 68.04) * mm, v(10.58, 68) * mm, v(10.56, 67.98) * mm]});
            skFitSpline(sketch, "E299", {"points": [v(10.56, 67.98) * mm, v(10.54, 67.95) * mm, v(10.51, 67.94) * mm, v(10.47, 67.94) * mm]});
            skFitSpline(sketch, "E300", {"points": [v(10.47, 67.94) * mm, v(10.44, 67.94) * mm, v(10.4, 67.95) * mm, v(10.39, 67.98) * mm]});
            skFitSpline(sketch, "E301", {"points": [v(10.39, 67.98) * mm, v(10.37, 68) * mm, v(10.36, 68.05) * mm, v(10.36, 68.1) * mm]});
            skFitSpline(sketch, "E302", {"points": [v(10.36, 68.1) * mm, v(10.36, 68.15) * mm, v(10.37, 68.18) * mm, v(10.39, 68.21) * mm]});
            skFitSpline(sketch, "E303", {"points": [v(10.39, 68.21) * mm, v(10.4, 68.24) * mm, v(10.44, 68.25) * mm, v(10.47, 68.25) * mm]});
            skLineSegment(sketch, "E304", {"start": v(10.01, 68.03) * mm, "end": v(10.01, 68.37) * mm});
            skLineSegment(sketch, "E305", {"start": v(10.01, 68.37) * mm, "end": v(9.83, 68.37) * mm});
            skLineSegment(sketch, "E306", {"start": v(9.83, 68.37) * mm, "end": v(9.83, 68.31) * mm});
            skFitSpline(sketch, "E307", {"points": [v(9.83, 68.31) * mm, v(9.83, 68.28) * mm, v(9.83, 68.24) * mm, v(9.83, 68.2) * mm]});
            skFitSpline(sketch, "E308", {"points": [v(9.83, 68.2) * mm, v(9.83, 68.15) * mm, v(9.83, 68.12) * mm, v(9.83, 68.1) * mm]});
            skFitSpline(sketch, "E309", {"points": [v(9.83, 68.1) * mm, v(9.83, 68.06) * mm, v(9.83, 68.03) * mm, v(9.83, 68) * mm]});
            skFitSpline(sketch, "E310", {"points": [v(9.83, 68) * mm, v(9.83, 68) * mm, v(9.82, 67.98) * mm, v(9.82, 67.97) * mm]});
            skFitSpline(sketch, "E311", {"points": [v(9.82, 67.97) * mm, v(9.8, 67.96) * mm, v(9.8, 67.95) * mm, v(9.79, 67.94) * mm]});
            skFitSpline(sketch, "E312", {"points": [v(9.79, 67.94) * mm, v(9.78, 67.93) * mm, v(9.76, 67.93) * mm, v(9.75, 67.93) * mm]});
            skFitSpline(sketch, "E313", {"points": [v(9.75, 67.93) * mm, v(9.7, 67.93) * mm, v(9.68, 67.94) * mm, v(9.66, 67.97) * mm]});
            skFitSpline(sketch, "E314", {"points": [v(9.66, 67.97) * mm, v(9.64, 68) * mm, v(9.63, 68.04) * mm, v(9.63, 68.1) * mm]});
            skLineSegment(sketch, "E315", {"start": v(9.63, 68.1) * mm, "end": v(9.63, 68.37) * mm});
            skLineSegment(sketch, "E316", {"start": v(9.63, 68.37) * mm, "end": v(9.45, 68.37) * mm});
            skLineSegment(sketch, "E317", {"start": v(9.45, 68.37) * mm, "end": v(9.45, 67.8) * mm});
            skLineSegment(sketch, "E318", {"start": v(9.45, 67.8) * mm, "end": v(9.63, 67.8) * mm});
            skLineSegment(sketch, "E319", {"start": v(9.63, 67.8) * mm, "end": v(9.63, 67.9) * mm});
            skFitSpline(sketch, "E320", {"points": [v(9.63, 67.9) * mm, v(9.65, 67.86) * mm, v(9.68, 67.83) * mm, v(9.71, 67.82) * mm]});
            skFitSpline(sketch, "E321", {"points": [v(9.71, 67.82) * mm, v(9.74, 67.8) * mm, v(9.78, 67.8) * mm, v(9.81, 67.8) * mm]});
            skFitSpline(sketch, "E322", {"points": [v(9.81, 67.8) * mm, v(9.88, 67.8) * mm, v(9.93, 67.82) * mm, v(9.96, 67.85) * mm]});
            skFitSpline(sketch, "E323", {"points": [v(9.96, 67.85) * mm, v(10, 67.9) * mm, v(10.01, 67.95) * mm, v(10.01, 68.03) * mm]});
            skLineSegment(sketch, "E324", {"start": v(8.72, 68.1) * mm, "end": v(8.72, 68.04) * mm});
            skLineSegment(sketch, "E325", {"start": v(8.72, 68.04) * mm, "end": v(9.14, 68.04) * mm});
            skFitSpline(sketch, "E326", {"points": [v(9.14, 68.04) * mm, v(9.13, 68) * mm, v(9.12, 67.97) * mm, v(9.1, 67.95) * mm]});
            skFitSpline(sketch, "E327", {"points": [v(9.1, 67.95) * mm, v(9.07, 67.92) * mm, v(9.03, 67.91) * mm, v(8.98, 67.91) * mm]});
            skFitSpline(sketch, "E328", {"points": [v(8.98, 67.91) * mm, v(8.95, 67.91) * mm, v(8.9, 67.92) * mm, v(8.87, 67.93) * mm]});
            skFitSpline(sketch, "E329", {"points": [v(8.87, 67.93) * mm, v(8.83, 67.94) * mm, v(8.79, 67.96) * mm, v(8.75, 67.98) * mm]});
            skLineSegment(sketch, "E330", {"start": v(8.75, 67.98) * mm, "end": v(8.75, 67.84) * mm});
            skFitSpline(sketch, "E331", {"points": [v(8.75, 67.84) * mm, v(8.79, 67.83) * mm, v(8.83, 67.82) * mm, v(8.87, 67.8) * mm]});
            skFitSpline(sketch, "E332", {"points": [v(8.87, 67.8) * mm, v(8.92, 67.8) * mm, v(8.96, 67.8) * mm, v(9, 67.8) * mm]});
            skFitSpline(sketch, "E333", {"points": [v(9, 67.8) * mm, v(9.1, 67.8) * mm, v(9.18, 67.82) * mm, v(9.24, 67.87) * mm]});
            skFitSpline(sketch, "E334", {"points": [v(9.24, 67.87) * mm, v(9.3, 67.92) * mm, v(9.32, 68) * mm, v(9.32, 68.09) * mm]});
            skFitSpline(sketch, "E335", {"points": [v(9.32, 68.09) * mm, v(9.32, 68.18) * mm, v(9.3, 68.25) * mm, v(9.24, 68.3) * mm]});
            skFitSpline(sketch, "E336", {"points": [v(9.24, 68.3) * mm, v(9.18, 68.36) * mm, v(9.1, 68.38) * mm, v(9, 68.38) * mm]});
            skFitSpline(sketch, "E337", {"points": [v(9, 68.38) * mm, v(8.92, 68.38) * mm, v(8.85, 68.35) * mm, v(8.8, 68.3) * mm]});
            skFitSpline(sketch, "E338", {"points": [v(8.8, 68.3) * mm, v(8.75, 68.25) * mm, v(8.72, 68.18) * mm, v(8.72, 68.1) * mm]});
            skFitSpline(sketch, "E339", {"points": [v(8.9, 68.15) * mm, v(8.9, 68.18) * mm, v(8.91, 68.21) * mm, v(8.93, 68.23) * mm]});
            skFitSpline(sketch, "E340", {"points": [v(8.93, 68.23) * mm, v(8.95, 68.25) * mm, v(8.98, 68.26) * mm, v(9.01, 68.26) * mm]});
            skFitSpline(sketch, "E341", {"points": [v(9.01, 68.26) * mm, v(9.04, 68.26) * mm, v(9.07, 68.25) * mm, v(9.1, 68.23) * mm]});
            skFitSpline(sketch, "E342", {"points": [v(9.1, 68.23) * mm, v(9.12, 68.21) * mm, v(9.13, 68.19) * mm, v(9.13, 68.15) * mm]});
            skLineSegment(sketch, "E343", {"start": v(9.13, 68.15) * mm, "end": v(8.9, 68.15) * mm});
            skLineSegment(sketch, "E344", {"start": v(8.15, 68.35) * mm, "end": v(8.15, 68.21) * mm});
            skFitSpline(sketch, "E345", {"points": [v(8.15, 68.21) * mm, v(8.19, 68.23) * mm, v(8.22, 68.24) * mm, v(8.26, 68.25) * mm]});
            skFitSpline(sketch, "E346", {"points": [v(8.26, 68.25) * mm, v(8.3, 68.26) * mm, v(8.33, 68.26) * mm, v(8.36, 68.26) * mm]});
            skFitSpline(sketch, "E347", {"points": [v(8.36, 68.26) * mm, v(8.4, 68.26) * mm, v(8.42, 68.26) * mm, v(8.44, 68.25) * mm]});
            skFitSpline(sketch, "E348", {"points": [v(8.44, 68.25) * mm, v(8.45, 68.24) * mm, v(8.46, 68.23) * mm, v(8.46, 68.21) * mm]});
            skFitSpline(sketch, "E349", {"points": [v(8.46, 68.21) * mm, v(8.46, 68.2) * mm, v(8.45, 68.19) * mm, v(8.44, 68.18) * mm]});
            skFitSpline(sketch, "E350", {"points": [v(8.44, 68.18) * mm, v(8.43, 68.17) * mm, v(8.4, 68.16) * mm, v(8.38, 68.16) * mm]});
            skLineSegment(sketch, "E351", {"start": v(8.38, 68.16) * mm, "end": v(8.34, 68.16) * mm});
            skFitSpline(sketch, "E352", {"points": [v(8.34, 68.16) * mm, v(8.25, 68.14) * mm, v(8.2, 68.13) * mm, v(8.16, 68.1) * mm]});
            skFitSpline(sketch, "E353", {"points": [v(8.16, 68.1) * mm, v(8.13, 68.07) * mm, v(8.11, 68.03) * mm, v(8.11, 67.97) * mm]});
            skFitSpline(sketch, "E354", {"points": [v(8.11, 67.97) * mm, v(8.11, 67.91) * mm, v(8.13, 67.87) * mm, v(8.18, 67.84) * mm]});
            skFitSpline(sketch, "E355", {"points": [v(8.18, 67.84) * mm, v(8.22, 67.81) * mm, v(8.29, 67.8) * mm, v(8.37, 67.8) * mm]});
            skFitSpline(sketch, "E356", {"points": [v(8.37, 67.8) * mm, v(8.41, 67.8) * mm, v(8.45, 67.8) * mm, v(8.49, 67.8) * mm]});
            skFitSpline(sketch, "E357", {"points": [v(8.49, 67.8) * mm, v(8.53, 67.81) * mm, v(8.57, 67.82) * mm, v(8.6, 67.83) * mm]});
            skLineSegment(sketch, "E358", {"start": v(8.6, 67.83) * mm, "end": v(8.6, 67.97) * mm});
            skFitSpline(sketch, "E359", {"points": [v(8.6, 67.97) * mm, v(8.57, 67.95) * mm, v(8.54, 67.94) * mm, v(8.5, 67.93) * mm]});
            skFitSpline(sketch, "E360", {"points": [v(8.5, 67.93) * mm, v(8.46, 67.92) * mm, v(8.43, 67.91) * mm, v(8.39, 67.91) * mm]});
            skFitSpline(sketch, "E361", {"points": [v(8.39, 67.91) * mm, v(8.35, 67.91) * mm, v(8.33, 67.92) * mm, v(8.3, 67.93) * mm]});
            skFitSpline(sketch, "E362", {"points": [v(8.3, 67.93) * mm, v(8.3, 67.94) * mm, v(8.28, 67.95) * mm, v(8.28, 67.97) * mm]});
            skFitSpline(sketch, "E363", {"points": [v(8.28, 67.97) * mm, v(8.28, 67.99) * mm, v(8.29, 68) * mm, v(8.3, 68) * mm]});
            skFitSpline(sketch, "E364", {"points": [v(8.3, 68) * mm, v(8.31, 68.01) * mm, v(8.34, 68.02) * mm, v(8.37, 68.03) * mm]});
            skLineSegment(sketch, "E365", {"start": v(8.37, 68.03) * mm, "end": v(8.4, 68.03) * mm});
            skFitSpline(sketch, "E366", {"points": [v(8.4, 68.03) * mm, v(8.48, 68.04) * mm, v(8.54, 68.06) * mm, v(8.57, 68.08) * mm]});
            skFitSpline(sketch, "E367", {"points": [v(8.57, 68.08) * mm, v(8.6, 68.11) * mm, v(8.62, 68.15) * mm, v(8.62, 68.2) * mm]});
            skFitSpline(sketch, "E368", {"points": [v(8.62, 68.2) * mm, v(8.62, 68.27) * mm, v(8.6, 68.3) * mm, v(8.56, 68.34) * mm]});
            skFitSpline(sketch, "E369", {"points": [v(8.56, 68.34) * mm, v(8.52, 68.37) * mm, v(8.46, 68.38) * mm, v(8.37, 68.38) * mm]});
            skFitSpline(sketch, "E370", {"points": [v(8.37, 68.38) * mm, v(8.34, 68.38) * mm, v(8.3, 68.38) * mm, v(8.27, 68.37) * mm]});
            skFitSpline(sketch, "E371", {"points": [v(8.27, 68.37) * mm, v(8.23, 68.37) * mm, v(8.2, 68.36) * mm, v(8.15, 68.35) * mm]});
            skLineSegment(sketch, "E372", {"start": v(7.54, 68.35) * mm, "end": v(7.54, 68.21) * mm});
            skFitSpline(sketch, "E373", {"points": [v(7.54, 68.21) * mm, v(7.58, 68.23) * mm, v(7.62, 68.24) * mm, v(7.65, 68.25) * mm]});
            skFitSpline(sketch, "E374", {"points": [v(7.65, 68.25) * mm, v(7.69, 68.26) * mm, v(7.72, 68.26) * mm, v(7.75, 68.26) * mm]});
            skFitSpline(sketch, "E375", {"points": [v(7.75, 68.26) * mm, v(7.79, 68.26) * mm, v(7.81, 68.26) * mm, v(7.83, 68.25) * mm]});
            skFitSpline(sketch, "E376", {"points": [v(7.83, 68.25) * mm, v(7.85, 68.24) * mm, v(7.85, 68.23) * mm, v(7.85, 68.21) * mm]});
            skFitSpline(sketch, "E377", {"points": [v(7.85, 68.21) * mm, v(7.85, 68.2) * mm, v(7.85, 68.19) * mm, v(7.83, 68.18) * mm]});
            skFitSpline(sketch, "E378", {"points": [v(7.83, 68.18) * mm, v(7.82, 68.17) * mm, v(7.8, 68.16) * mm, v(7.77, 68.16) * mm]});
            skLineSegment(sketch, "E379", {"start": v(7.77, 68.16) * mm, "end": v(7.74, 68.16) * mm});
            skFitSpline(sketch, "E380", {"points": [v(7.74, 68.16) * mm, v(7.65, 68.14) * mm, v(7.58, 68.13) * mm, v(7.55, 68.1) * mm]});
            skFitSpline(sketch, "E381", {"points": [v(7.55, 68.1) * mm, v(7.52, 68.07) * mm, v(7.5, 68.03) * mm, v(7.5, 67.97) * mm]});
            skFitSpline(sketch, "E382", {"points": [v(7.5, 67.97) * mm, v(7.5, 67.91) * mm, v(7.53, 67.87) * mm, v(7.57, 67.84) * mm]});
            skFitSpline(sketch, "E383", {"points": [v(7.57, 67.84) * mm, v(7.61, 67.81) * mm, v(7.68, 67.8) * mm, v(7.77, 67.8) * mm]});
            skFitSpline(sketch, "E384", {"points": [v(7.77, 67.8) * mm, v(7.8, 67.8) * mm, v(7.84, 67.8) * mm, v(7.88, 67.8) * mm]});
            skFitSpline(sketch, "E385", {"points": [v(7.88, 67.8) * mm, v(7.92, 67.81) * mm, v(7.96, 67.82) * mm, v(8, 67.83) * mm]});
            skLineSegment(sketch, "E386", {"start": v(8, 67.83) * mm, "end": v(8, 67.97) * mm});
            skFitSpline(sketch, "E387", {"points": [v(8, 67.97) * mm, v(7.97, 67.95) * mm, v(7.93, 67.94) * mm, v(7.9, 67.93) * mm]});
            skFitSpline(sketch, "E388", {"points": [v(7.9, 67.93) * mm, v(7.86, 67.92) * mm, v(7.82, 67.91) * mm, v(7.78, 67.91) * mm]});
            skFitSpline(sketch, "E389", {"points": [v(7.78, 67.91) * mm, v(7.74, 67.91) * mm, v(7.72, 67.92) * mm, v(7.7, 67.93) * mm]});
            skFitSpline(sketch, "E390", {"points": [v(7.7, 67.93) * mm, v(7.68, 67.94) * mm, v(7.67, 67.95) * mm, v(7.67, 67.97) * mm]});
            skFitSpline(sketch, "E391", {"points": [v(7.67, 67.97) * mm, v(7.67, 67.99) * mm, v(7.68, 68) * mm, v(7.7, 68) * mm]});
            skFitSpline(sketch, "E392", {"points": [v(7.7, 68) * mm, v(7.7, 68.01) * mm, v(7.73, 68.02) * mm, v(7.76, 68.03) * mm]});
            skLineSegment(sketch, "E393", {"start": v(7.76, 68.03) * mm, "end": v(7.8, 68.03) * mm});
            skFitSpline(sketch, "E394", {"points": [v(7.8, 68.03) * mm, v(7.88, 68.04) * mm, v(7.93, 68.06) * mm, v(7.96, 68.08) * mm]});
            skFitSpline(sketch, "E395", {"points": [v(7.96, 68.08) * mm, v(8, 68.11) * mm, v(8.01, 68.15) * mm, v(8.01, 68.2) * mm]});
            skFitSpline(sketch, "E396", {"points": [v(8.01, 68.2) * mm, v(8.01, 68.27) * mm, v(8, 68.3) * mm, v(7.95, 68.34) * mm]});
            skFitSpline(sketch, "E397", {"points": [v(7.95, 68.34) * mm, v(7.9, 68.37) * mm, v(7.85, 68.38) * mm, v(7.76, 68.38) * mm]});
            skFitSpline(sketch, "E398", {"points": [v(7.76, 68.38) * mm, v(7.73, 68.38) * mm, v(7.7, 68.38) * mm, v(7.66, 68.37) * mm]});
            skFitSpline(sketch, "E399", {"points": [v(7.66, 68.37) * mm, v(7.62, 68.37) * mm, v(7.58, 68.36) * mm, v(7.54, 68.35) * mm]});
            skLineSegment(sketch, "E400", {"start": v(7.35, 68) * mm, "end": v(7.17, 68) * mm});
            skLineSegment(sketch, "E401", {"start": v(7.17, 68) * mm, "end": v(7.17, 67.8) * mm});
            skLineSegment(sketch, "E402", {"start": v(7.17, 67.8) * mm, "end": v(7.35, 67.8) * mm});
            skLineSegment(sketch, "E403", {"start": v(7.35, 67.8) * mm, "end": v(7.35, 68) * mm});
            skSolve(sketch);
        }
        {
            var Q0;
            Q0=qSketchRegion(id+"F2",true);
            extrude(context, id + "F3", {"entities" : qUnion([Q0]), "operationType" : NewBodyOperationType.ADD, "depth" : 2 * mm, "offsetDistance" : 25 * mm});
        }
    });
